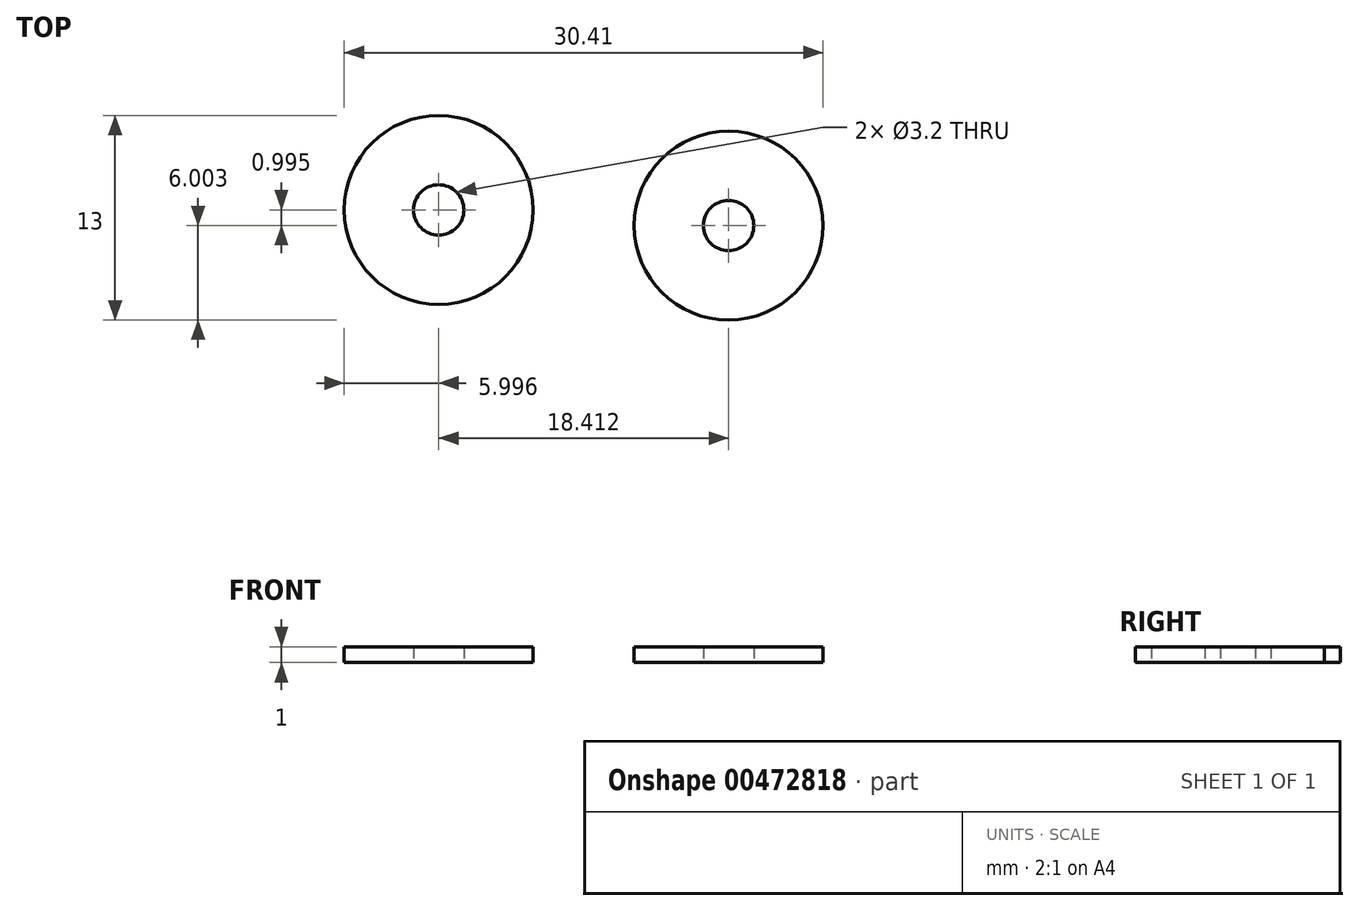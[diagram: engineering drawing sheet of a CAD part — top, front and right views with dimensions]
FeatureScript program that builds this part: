
annotation { "Feature Type Name" : "Feature", "Feature Type Description" : "" }
export const myFeature = defineFeature(function(context is Context, id is Id, definition is map)
    precondition{}
    {
        {
            var Q0;
            Q0=qCreatedBy(makeId("Top.planeOp"),FACE);
            var sketch = newSketch(context, id + "F0", { "sketchPlane" : qUnion([Q0])});
            skCircle(sketch, "E0", {"center": v(12.32, -17.54) * mm, "radius": 6 * mm});
            skCircle(sketch, "E1", {"center": v(30.73, -18.54) * mm, "radius": 6 * mm});
            skCircle(sketch, "E2", {"center": v(12.32, -17.54) * mm, "radius": 1.6 * mm});
            skCircle(sketch, "E3", {"center": v(30.73, -18.54) * mm, "radius": 1.6 * mm});
            skSolve(sketch);
        }
        {
            var Q0;
            Q0=makeQuery(id+"F0.imprint","IMPRINT",FACE,{"disambiguationData":[TD([[makeQuery(id+"F0.imprint","IMPRINT",EDGE,{"derivedFrom":sQuery(id+"F0.wireOp",EDGE,"E0")}),1.0]])]});
            var Q1;
            Q1=makeQuery(id+"F0.imprint","IMPRINT",FACE,{"disambiguationData":[TD([[makeQuery(id+"F0.imprint","IMPRINT",EDGE,{"derivedFrom":sQuery(id+"F0.wireOp",EDGE,"E1")}),1.0]])]});
            extrude(context, id + "F1", {"entities" : qUnion([Q0, Q1]), "depth" : 1 * mm});
        }
    });
